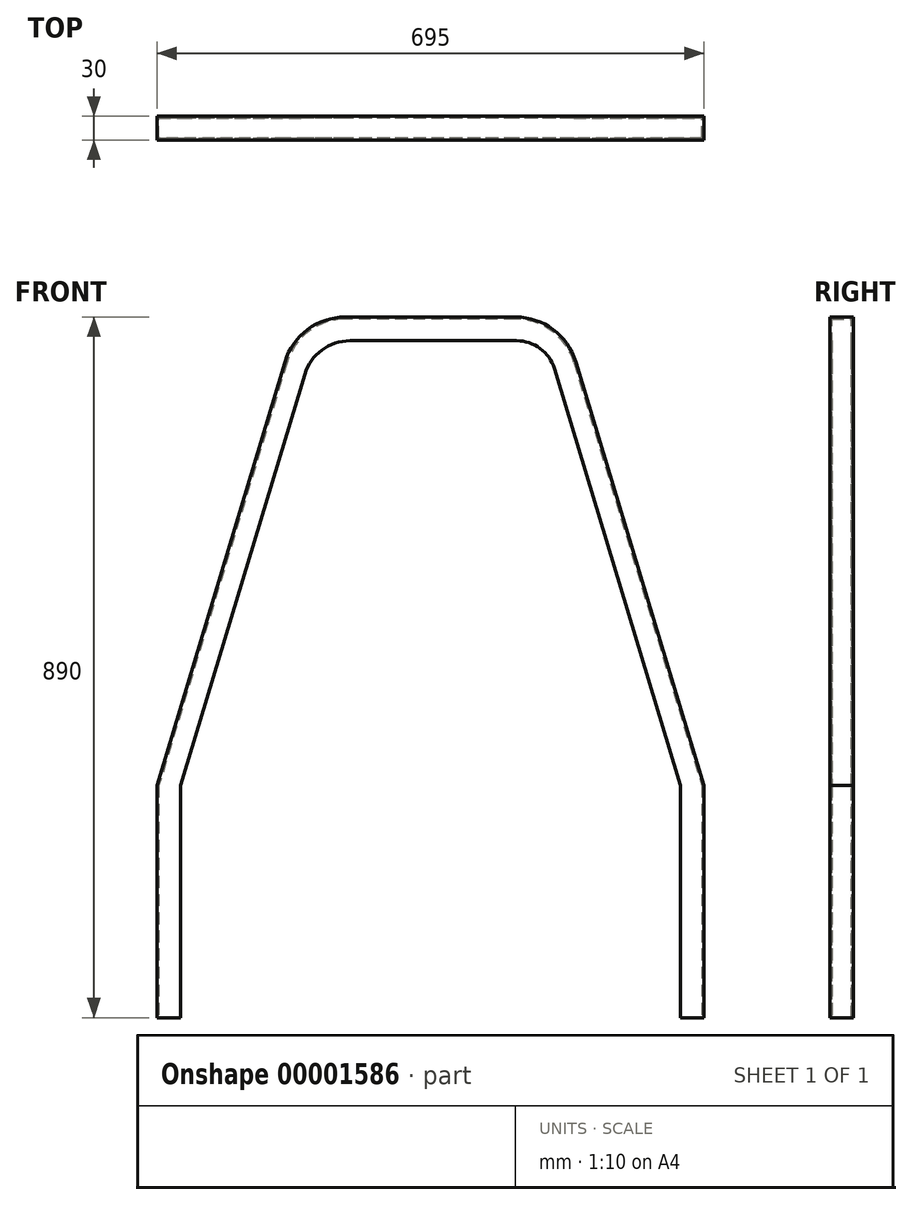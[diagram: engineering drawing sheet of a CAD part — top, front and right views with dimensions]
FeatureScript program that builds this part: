
annotation { "Feature Type Name" : "Feature", "Feature Type Description" : "" }
export const myFeature = defineFeature(function(context is Context, id is Id, definition is map)
    precondition{}
    {
        {
            var Q0;
            Q0=qCreatedBy(makeId("Front.planeOp"),FACE);
            var sketch = newSketch(context, id + "F0", { "sketchPlane" : qUnion([Q0])});
            skLineSegment(sketch, "E0", {"start": v(-184.8, 537.98) * mm, "end": v(-347.5, 0) * mm});
            skLineSegment(sketch, "E1", {"start": v(-347.5, 0) * mm, "end": v(-347.5, -295.18) * mm});
            skLineSegment(sketch, "E2", {"start": v(-347.5, -295.18) * mm, "end": v(-317.5, -295.18) * mm});
            skLineSegment(sketch, "E3", {"start": v(-317.5, -295.18) * mm, "end": v(-317.5, 0) * mm});
            skLineSegment(sketch, "E4", {"start": v(-317.5, 0) * mm, "end": v(-159.57, 522.19) * mm});
            skLineSegment(sketch, "E5", {"start": v(-102.14, 564.82) * mm, "end": v(0, 564.82) * mm});
            skLineSegment(sketch, "E6", {"start": v(-108.22, 594.82) * mm, "end": v(0, 594.82) * mm});
            skLineSegment(sketch, "E7", {"start": v(0, 594.82) * mm, "end": v(0, -351.6) * mm, "construction": true});
            skLineSegment(sketch, "E8.0.MirrorCS", {"start": v(347.5, -295.18) * mm, "end": v(317.5, -295.18) * mm});
            skLineSegment(sketch, "E8.1.MirrorCS", {"start": v(317.5, -295.18) * mm, "end": v(317.5, 0) * mm});
            skLineSegment(sketch, "E8.2.MirrorCS", {"start": v(317.5, 0) * mm, "end": v(157.42, 529.3) * mm});
            skLineSegment(sketch, "E8.3.MirrorCS", {"start": v(109.56, 564.82) * mm, "end": v(0, 564.82) * mm});
            skLineSegment(sketch, "E8.4.MirrorCS", {"start": v(184.8, 537.98) * mm, "end": v(347.5, 0) * mm});
            skLineSegment(sketch, "E8.5.MirrorCS", {"start": v(108.22, 594.82) * mm, "end": v(0, 594.82) * mm});
            skLineSegment(sketch, "E8.6.MirrorCS", {"start": v(347.5, 0) * mm, "end": v(347.5, -295.18) * mm});
            skPoint(sketch, "E9.visualSharp", {"position": v(-146.68, 564.82) * mm});
            skArc(sketch, "E9.filletArc", {"start": v(-102.14, 564.82) * mm, "mid": v(-137.9, 553) * mm, "end": v(-159.57, 522.19) * mm});
            skPoint(sketch, "E10.visualSharp", {"position": v(146.68, 564.82) * mm});
            skArc(sketch, "E10.filletArc", {"start": v(157.42, 529.3) * mm, "mid": v(139.36, 554.97) * mm, "end": v(109.56, 564.82) * mm});
            skPoint(sketch, "E11.visualSharp", {"position": v(167.6, 594.82) * mm});
            skArc(sketch, "E11.filletArc", {"start": v(184.8, 537.98) * mm, "mid": v(155.9, 579.05) * mm, "end": v(108.22, 594.82) * mm});
            skPoint(sketch, "E12.visualSharp", {"position": v(-167.6, 594.82) * mm});
            skArc(sketch, "E12.filletArc", {"start": v(-108.22, 594.82) * mm, "mid": v(-155.9, 579.05) * mm, "end": v(-184.8, 537.98) * mm});
            skSolve(sketch);
        }
        {
            var Q0;
            Q0 = qSketchRegion(id + "F0", true);
            extrude(context, id + "F1", {"entities" : qUnion([Q0]), "depth" : 30 * mm});
        }
        {
            var Q0;
            Q0=makeQuery(id+"F1.opExtrude","SWEPT_FACE",FACE,{"disambiguationData":[OSD([sQuery(id+"F0.wireOp",EDGE,"E8.1.MirrorCS")])]});
            var Q1;
            Q1=makeQuery(id+"F1.opExtrude","SWEPT_FACE",FACE,{"disambiguationData":[OSD([sQuery(id+"F0.wireOp",EDGE,"E8.2.MirrorCS")])]});
            var Q2;
            Q2=makeQuery(id+"F1.opExtrude","SWEPT_FACE",FACE,{"disambiguationData":[OSD([sQuery(id+"F0.wireOp",EDGE,"E10.filletArc")])]});
            var Q3;
            Q3=makeQuery(id+"F1.opExtrude","SWEPT_FACE",FACE,{"disambiguationData":[OSD([sQuery(id+"F0.wireOp",EDGE,"E5")])]});
            var Q4;
            Q4=makeQuery(id+"F1.opExtrude","SWEPT_FACE",FACE,{"disambiguationData":[OSD([sQuery(id+"F0.wireOp",EDGE,"E9.filletArc")])]});
            var Q5;
            Q5=makeQuery(id+"F1.opExtrude","SWEPT_FACE",FACE,{"disambiguationData":[OSD([sQuery(id+"F0.wireOp",EDGE,"E4")])]});
            var Q6;
            Q6=makeQuery(id+"F1.opExtrude","SWEPT_FACE",FACE,{"disambiguationData":[OSD([sQuery(id+"F0.wireOp",EDGE,"E3")])]});
            var Q7;
            Q7=makeQuery(id+"F1.opExtrude","SWEPT_FACE",FACE,{"disambiguationData":[OSD([sQuery(id+"F0.wireOp",EDGE,"E8.0.MirrorCS")])]});
            var Q8;
            Q8=makeQuery(id+"F1.opExtrude","SWEPT_FACE",FACE,{"disambiguationData":[OSD([sQuery(id+"F0.wireOp",EDGE,"E2")])]});
            shell(context, id + "F2", {"entities" : qUnion([Q0, Q1, Q2, Q3, Q4, Q5, Q6, Q7, Q8]), "thickness" : 2.5 * mm});
        }
    });
